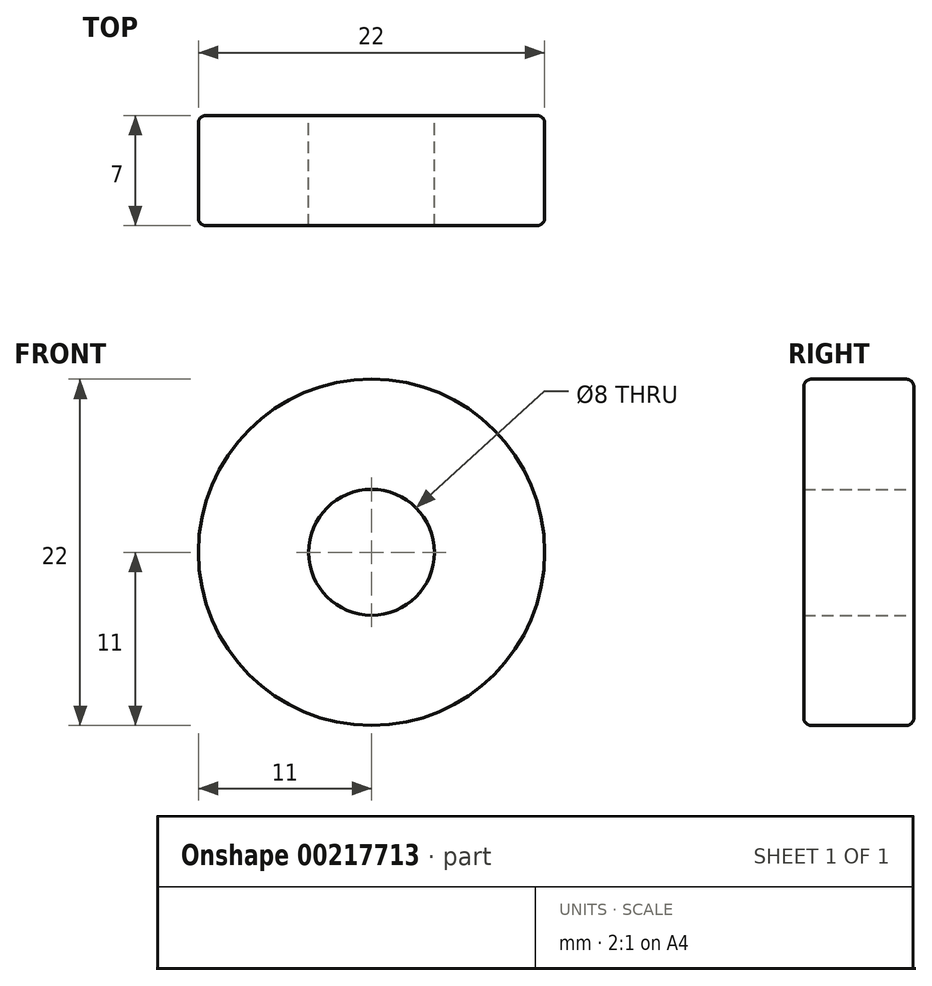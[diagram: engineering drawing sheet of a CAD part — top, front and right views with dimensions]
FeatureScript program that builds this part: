
annotation { "Feature Type Name" : "Feature", "Feature Type Description" : "" }
export const myFeature = defineFeature(function(context is Context, id is Id, definition is map)
    precondition{}
    {
        {
            var Q0;
            Q0=qCreatedBy(makeId("Front.planeOp"),FACE);
            var sketch = newSketch(context, id + "F0", { "sketchPlane" : qUnion([Q0])});
            skCircle(sketch, "E0", {"center": v(0, 0) * mm, "radius": 4 * mm});
            skCircle(sketch, "E1", {"center": v(0, 0) * mm, "radius": 11 * mm});
            skSolve(sketch);
        }
        {
            var Q0;
            Q0=makeQuery(id+"F0.imprint","IMPRINT",FACE,{"disambiguationData":[TD([[makeQuery(id+"F0.imprint","IMPRINT",EDGE,{"derivedFrom":sQuery(id+"F0.wireOp",EDGE,"E0")}),-1.0]])]});
            extrude(context, id + "F1", {"entities" : qUnion([Q0]), "depth" : 7 * mm, "symmetric" : true});
        }
        {
            var Q0;
            Q0=makeQuery(id+"F1.opExtrude","CAP_EDGE",EDGE,{"disambiguationData":[OSD([sQuery(id+"F0.wireOp",EDGE,"E1")])],"isStart":false});
            var Q1;
            Q1=makeQuery(id+"F1.opExtrude","CAP_EDGE",EDGE,{"disambiguationData":[OSD([sQuery(id+"F0.wireOp",EDGE,"E1")])],"isStart":true});
            fillet(context, id + "F2", {"entities" : qUnion([Q0, Q1]), "radius" : .5 * mm, "tangentPropagation" : true, "allowEdgeOverflow" : false});
        }
    });
